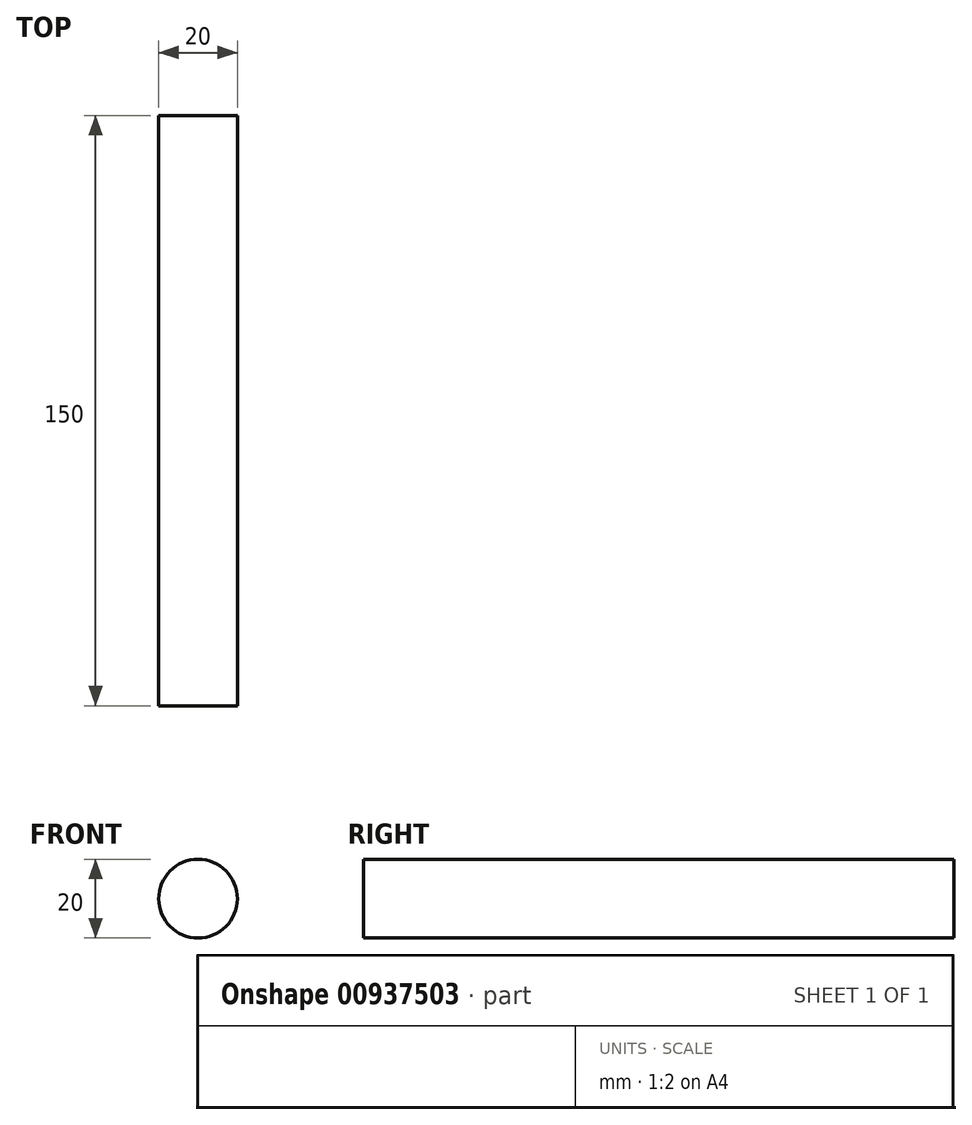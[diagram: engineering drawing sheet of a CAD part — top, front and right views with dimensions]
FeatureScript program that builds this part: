
annotation { "Feature Type Name" : "Feature", "Feature Type Description" : "" }
export const myFeature = defineFeature(function(context is Context, id is Id, definition is map)
    precondition{}
    {
        {
            var Q0;
            Q0=qCreatedBy(makeId("Front.planeOp"),FACE);
            var sketch = newSketch(context, id + "F0", { "sketchPlane" : qUnion([Q0])});
            skCircle(sketch, "E0", {"center": v(0, 0) * mm, "radius": 10 * mm});
            skSolve(sketch);
        }
        {
            var Q0;
            Q0=makeQuery(id+"F0.imprint","IMPRINT",FACE,{"disambiguationData":[TD([[makeQuery(id+"F0.imprint","IMPRINT",EDGE,{"derivedFrom":sQuery(id+"F0.wireOp",EDGE,"E0")}),1.0]])]});
            extrude(context, id + "F1", {"entities" : qUnion([Q0]), "depth" : 150 * mm, "offsetDistance" : 25 * mm});
        }
    });
